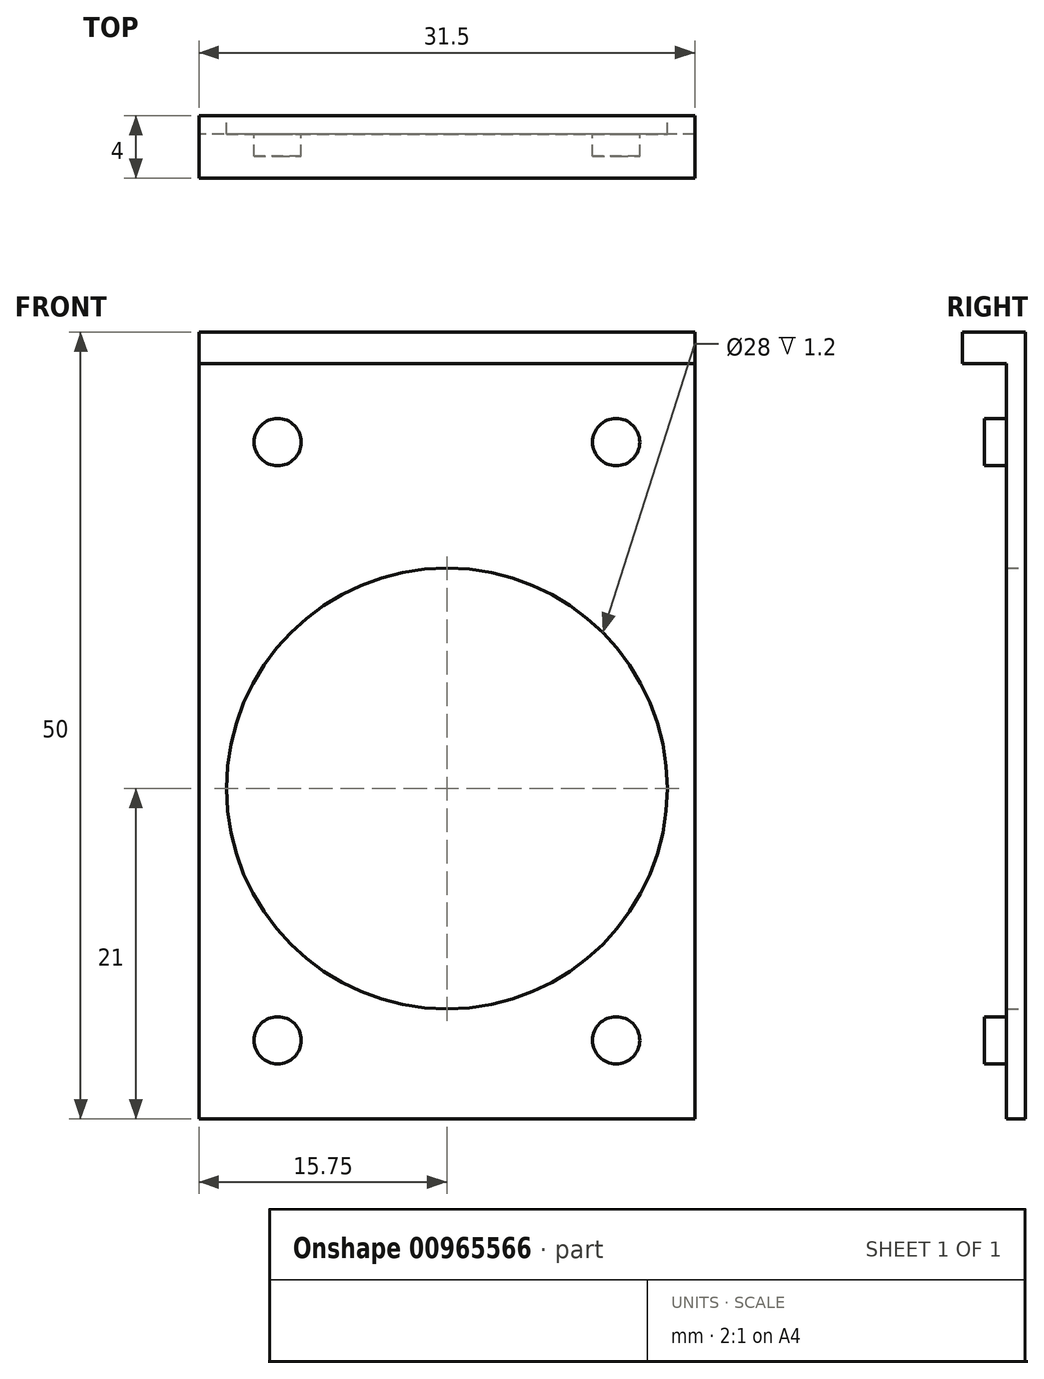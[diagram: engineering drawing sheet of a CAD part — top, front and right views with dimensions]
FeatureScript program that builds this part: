
annotation { "Feature Type Name" : "Feature", "Feature Type Description" : "" }
export const myFeature = defineFeature(function(context is Context, id is Id, definition is map)
    precondition{}
    {
        {
            var Q0;
            Q0=qCreatedBy(makeId("Front.planeOp"),FACE);
            var sketch = newSketch(context, id + "F0", { "sketchPlane" : qUnion([Q0])});
            skLineSegment(sketch, "E0.bottom", {"start": v(-15.75, 25) * mm, "end": v(15.75, 25) * mm});
            skLineSegment(sketch, "E0.top", {"start": v(-15.75, -25) * mm, "end": v(15.75, -25) * mm});
            skLineSegment(sketch, "E0.left", {"start": v(-15.75, 25) * mm, "end": v(-15.75, -25) * mm});
            skLineSegment(sketch, "E0.right", {"start": v(15.75, 25) * mm, "end": v(15.75, -25) * mm});
            skLineSegment(sketch, "E1", {"start": v(15.75, 13.12) * mm, "end": v(0, 13.12) * mm, "construction": true});
            skLineSegment(sketch, "E2", {"start": v(0, -25) * mm, "end": v(0, -4) * mm, "construction": true});
            skCircle(sketch, "E3", {"center": v(0, -4) * mm, "radius": 14 * mm});
            skLineSegment(sketch, "E4.top", {"start": v(-15.75, 23) * mm, "end": v(15.75, 23) * mm});
            skLineSegment(sketch, "E4.left", {"start": v(-15.75, 25) * mm, "end": v(-15.75, 23) * mm});
            skLineSegment(sketch, "E4.right", {"start": v(15.75, 25) * mm, "end": v(15.75, 23) * mm});
            skLineSegment(sketch, "E5.bottom", {"start": v(-15.75, -25) * mm, "end": v(-10.75, -25) * mm, "construction": true});
            skLineSegment(sketch, "E5.top", {"start": v(-15.75, -20) * mm, "end": v(-10.75, -20) * mm, "construction": true});
            skLineSegment(sketch, "E5.left", {"start": v(-15.75, -25) * mm, "end": v(-15.75, -20) * mm, "construction": true});
            skLineSegment(sketch, "E5.right", {"start": v(-10.75, -25) * mm, "end": v(-10.75, -20) * mm, "construction": true});
            skLineSegment(sketch, "E6.bottom", {"start": v(15.75, -25) * mm, "end": v(10.75, -25) * mm, "construction": true});
            skLineSegment(sketch, "E6.top", {"start": v(15.75, -20) * mm, "end": v(10.75, -20) * mm, "construction": true});
            skLineSegment(sketch, "E6.left", {"start": v(15.75, -25) * mm, "end": v(15.75, -20) * mm, "construction": true});
            skLineSegment(sketch, "E6.right", {"start": v(10.75, -25) * mm, "end": v(10.75, -20) * mm, "construction": true});
            skLineSegment(sketch, "E7.bottom", {"start": v(-15.75, 23) * mm, "end": v(-10.75, 23) * mm, "construction": true});
            skLineSegment(sketch, "E7.top", {"start": v(-15.75, 18) * mm, "end": v(-10.75, 18) * mm, "construction": true});
            skLineSegment(sketch, "E7.left", {"start": v(-15.75, 23) * mm, "end": v(-15.75, 18) * mm, "construction": true});
            skLineSegment(sketch, "E7.right", {"start": v(-10.75, 23) * mm, "end": v(-10.75, 18) * mm, "construction": true});
            skLineSegment(sketch, "E8.bottom", {"start": v(15.75, 23) * mm, "end": v(10.75, 23) * mm, "construction": true});
            skLineSegment(sketch, "E8.left", {"start": v(15.75, 23) * mm, "end": v(15.75, 18) * mm, "construction": true});
            skLineSegment(sketch, "E9.top", {"start": v(15.75, 18) * mm, "end": v(10.75, 18) * mm, "construction": true});
            skLineSegment(sketch, "E9.right", {"start": v(10.75, 23) * mm, "end": v(10.75, 18) * mm, "construction": true});
            skCircle(sketch, "E10", {"center": v(-10.75, 18) * mm, "radius": 1.5 * mm});
            skCircle(sketch, "E11", {"center": v(10.75, 18) * mm, "radius": 1.5 * mm});
            skCircle(sketch, "E12", {"center": v(-10.75, -20) * mm, "radius": 1.5 * mm});
            skCircle(sketch, "E13", {"center": v(10.75, -20) * mm, "radius": 1.5 * mm});
            skSolve(sketch);
        }
        {
            var Q0;
            Q0=makeQuery(id+"F0.imprint","IMPRINT",FACE,{"disambiguationData":[TD([[makeQuery(id+"F0.imprint","IMPRINT",EDGE,{"derivedFrom":sQuery(id+"F0.wireOp",EDGE,"E0.top")}),1.0]])]});
            extrude(context, id + "F1", {"entities" : qUnion([Q0]), "depth" : 1.2 * mm, "offsetDistance" : 25 * mm});
        }
        {
            var Q0;
            Q0=makeQuery(id+"F0.imprint","IMPRINT",FACE,{"disambiguationData":[TD([[makeQuery(id+"F0.imprint","IMPRINT",EDGE,{"derivedFrom":sQuery(id+"F0.wireOp",EDGE,"E0.bottom")}),-1.0]])]});
            extrude(context, id + "F2", {"entities" : qUnion([Q0]), "operationType" : NewBodyOperationType.ADD, "depth" : 1.2 * mm, "offsetDistance" : 25 * mm});
        }
        {
            var Q0;
            Q0=makeQuery(id+"F0.imprint","IMPRINT",FACE,{"disambiguationData":[TD([[makeQuery(id+"F0.imprint","IMPRINT",EDGE,{"derivedFrom":sQuery(id+"F0.wireOp",EDGE,"E10")}),1.0]])]});
            var Q1;
            Q1=makeQuery(id+"F0.imprint","IMPRINT",FACE,{"disambiguationData":[TD([[makeQuery(id+"F0.imprint","IMPRINT",EDGE,{"derivedFrom":sQuery(id+"F0.wireOp",EDGE,"E11")}),1.0]])]});
            var Q2;
            Q2=makeQuery(id+"F0.imprint","IMPRINT",FACE,{"disambiguationData":[TD([[makeQuery(id+"F0.imprint","IMPRINT",EDGE,{"derivedFrom":sQuery(id+"F0.wireOp",EDGE,"E13")}),1.0]])]});
            var Q3;
            Q3=makeQuery(id+"F0.imprint","IMPRINT",FACE,{"disambiguationData":[TD([[makeQuery(id+"F0.imprint","IMPRINT",EDGE,{"derivedFrom":sQuery(id+"F0.wireOp",EDGE,"E12")}),1.0]])]});
            extrude(context, id + "F3", {"entities" : qUnion([Q0, Q1, Q2, Q3]), "operationType" : NewBodyOperationType.ADD, "depth" : 2.6 * mm, "offsetDistance" : 25 * mm});
        }
        {
            var Q0;
            Q0=makeQuery(id+"F0.imprint","IMPRINT",FACE,{"disambiguationData":[TD([[makeQuery(id+"F0.imprint","IMPRINT",EDGE,{"derivedFrom":sQuery(id+"F0.wireOp",EDGE,"E0.bottom")}),-1.0]])]});
            extrude(context, id + "F4", {"entities" : qUnion([Q0]), "operationType" : NewBodyOperationType.ADD, "depth" : 4 * mm, "offsetDistance" : 25 * mm});
        }
    });
